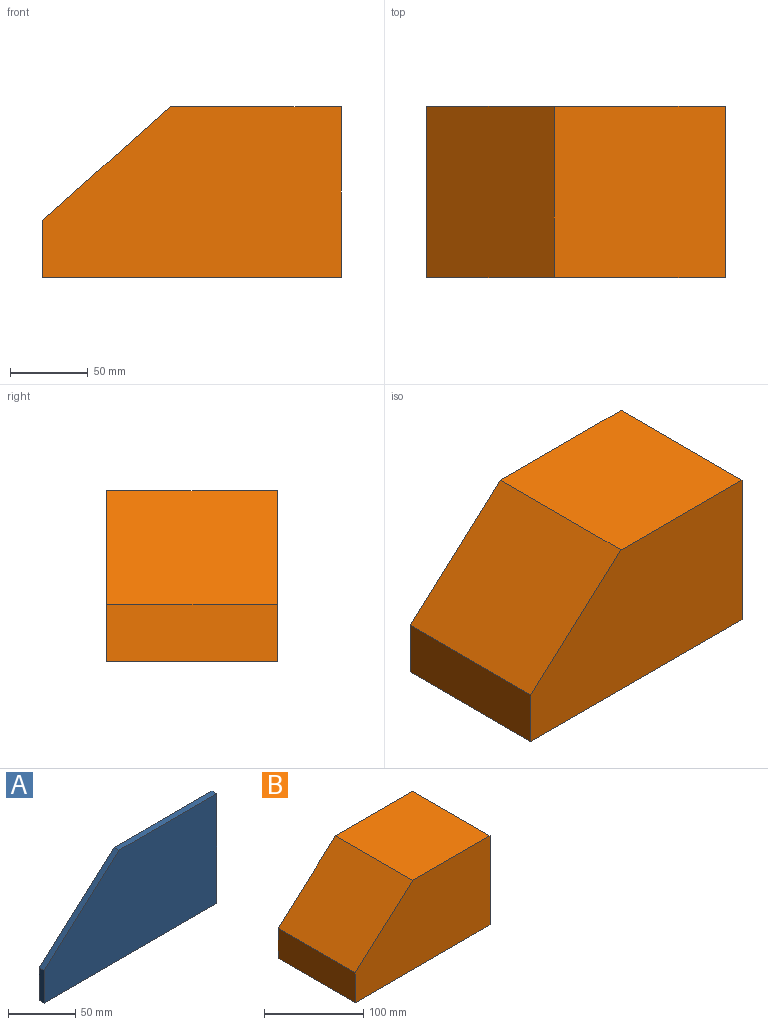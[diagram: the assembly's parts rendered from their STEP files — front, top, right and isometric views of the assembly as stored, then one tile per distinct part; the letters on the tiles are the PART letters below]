
ASSEMBLY  parts=2 mates=1
PART A: 7 faces, bbox 182.1x5x100 mm
  f0: plane 29.51x5mm, normal (-1,0,0), area 147.6mm2, adj f1,f4,f5,f6
  f1: plane 182.07x5mm, normal (0,0,-1), area 910.3mm2, adj f0,f2,f5,f6
  f2: plane 100x5mm, normal (1,0,0), area 500mm2, adj f1,f3,f5,f6
  f3: plane 103.09x5mm, normal (0,0,1), area 515.5mm2, adj f2,f4,f5,f6
  f4: plane 78.97x70.49mm, normal (-0.67,0,0.75), area 529.3mm2, adj f0,f3,f5,f6
  f5: plane 182.07x100mm, normal (0,-1,0), area 15423.4mm2, adj f0,f1,f2,f3,f4
  f6: plane 182.07x100mm, normal (0,1,0), area 15423.4mm2, adj f0,f1,f2,f3,f4
PART B: 25 faces, bbox 192.1x110x110 mm
  f0: plane 105x100mm, normal (-1,0,0), area 9866.5mm2, adj f1,f3,f10,f14,f15,f20,f22
  f1: plane 182.07x105mm, normal (0,0,1), area 18238.6mm2, adj f0,f2,f10,f12,f13,f20,f21
  f2: plane 105x29.51mm, normal (1,0,0), area 2813.7mm2, adj f1,f8,f10,f19,f20,f24
  f3: plane 105x103.09mm, normal (0,0,-1), area 9946.4mm2, adj f0,f8,f10,f16,f17,f20,f23
  f4: plane 192.07x110mm, normal (0,0,-1), area 21127.3mm2, adj f5,f9,f10,f11
  f5: plane 110x110mm, normal (1,0,0), area 12100mm2, adj f4,f6,f10,f11
  f6: plane 110x110mm, normal (0,0,1), area 12100mm2, adj f5,f7,f10,f11
  f7: plane 110x82.07mm, normal (-0.67,0,0.75), area 12100mm2, adj f6,f9,f10,f11
  f8: plane 105x78.97mm, normal (0.67,0,-0.75), area 10864mm2, adj f2,f3,f10,f18,f20,f24
  f9: plane 110x36.75mm, normal (-1,0,0), area 4042.8mm2, adj f4,f7,f10,f11
  f10: plane 192.07x110mm, normal (0,1,0), area 2698.4mm2, adj f0,f1,f2,f3,f4,f5,f6,f7
  f11: plane 192.07x110mm, normal (0,-1,0), area 18121.7mm2, adj f4,f5,f6,f7,f9
  f12: plane 110.64x100mm, normal (0.48,0,-0.88), area 12622.6mm2, adj f1,f13,f20,f21
  f13: plane 100x62.65mm, normal (-0.7,0,-0.72), area 8727.7mm2, adj f1,f12,f20,f21
  f14: plane 100x61.65mm, normal (0.7,0,0.72), area 8589.1mm2, adj f0,f15,f20,f22
  f15: plane 100x61.65mm, normal (0.48,0,-0.88), area 7034mm2, adj f0,f14,f20,f22
  f16: plane 100x60.21mm, normal (-0.48,0,0.88), area 6869.9mm2, adj f3,f17,f20,f23
  f17: plane 100x34.1mm, normal (0.7,0,0.72), area 4750.1mm2, adj f3,f16,f20,f23
  f18: plane 100x34.97mm, normal (-0.7,0,-0.72), area 4872mm2, adj f8,f19,f20,f24
  f19: plane 112.07x100mm, normal (-0.48,0,0.88), area 12786.7mm2, adj f2,f18,f20,f24
  f20: plane 182.07x100mm, normal (0,1,0), area 1706.5mm2, adj f0,f1,f2,f3,f8,f12,f13,f14
  f21: plane 173.28x60.77mm, normal (0,1,0), area 5264.9mm2, adj f1,f12,f13
  f22: plane 93.67x61.65mm, normal (0,1,0), area 2887.3mm2, adj f0,f14,f15
  f23: plane 94.31x33.07mm, normal (0,1,0), area 1559.5mm2, adj f3,f16,f17
  f24: plane 112.07x95.48mm, normal (0,1,0), area 4005.1mm2, adj f2,f8,f18,f19
PLACE A t=(0,110,0)mm
PLACE B at identity fixed
MATE fastened A.f5 <-> B.f20  axis (0,-1,0) through (-5,105,5)mm
